# Revit family: v-180sz5(-n)_50Hz
name_source: partatom
category: 機械設備
units: mm (PartAtom-declared; Revit-internal decimal feet)

## family parameters
OmniClass タイトル = Centrifugal Fans
OmniClass 番号 = 23.75.35.17.27
パーツ タイプ = 標準
ロード時にボイドで切り取り = いいえ
丸型コネクタ寸法 = 直径を使用
作業面ベース = いいえ
共有 = いいえ
常に垂直 = はい
部屋計算ポイント = はい

## types (1)
- V-180SZU5-N
    Cover_Width = 132  [stored 0.433071 ft]
    D1 = 475  [stored 1.5584 ft]
    D2 = 120  [stored 0.393701 ft]
    Depth = 304  [stored 0.997375 ft]
    Duct_EA_Depth = 113  [stored 0.370735 ft]
    Duct_H = 116  [stored 0.380577 ft]
    Duct_RA_Depth1 = 198  [stored 0.649606 ft]
    Duct_RA_Depth2 = 322  [stored 1.05643 ft]
    Duct_RA_W1 = 113  [stored 0.370735 ft]
    EAサイズ_D = 98  [stored 0.321522 ft]
    Gril_D = 73  [stored 0.239501 ft]
    Gril_Depth = 146  [stored 0.479003 ft]
    Gril_W = 155  [stored 0.50853 ft]
    Gril_Width = 61  [stored 0.200131 ft]
    H1 = 12  [stored 0.0393701 ft]
    H2 = 198  [stored 0.649606 ft]
    Height = 211  [stored 0.692257 ft]
    IfcExportAs = IfcFanType
    IfcExportType = PROPELLORAXIAL
    MAX静圧 = 178.0 Pa
    MAX風量 = 225.0 m³/h
    MID静圧 = 0.0 Pa
    MID風量 = 0.0 m³/h
    MIN静圧 = 12.5 Pa
    MIN風量 = 60.0 m³/h
    OmniClassCode = 23-33 31 19 11 15
    Panel_W = 35  [stored 0.114829 ft]
    RAサイズ_D = 98  [stored 0.321522 ft]
    URL = https://www.mitsubishielectric.co.jp
    Uniclass2015Code = Pr_65_67_29_12
    Uniclass2015Title = Centrifugal fans
    Uniclass2015Version = Systems v1.9
    W1 = 475  [stored 1.5584 ft]
    W2 = 110  [stored 0.360892 ft]
    W3 = 152  [stored 0.498688 ft]
    Width = 304  [stored 0.997375 ft]
    カバーマテリアル = 合成樹脂(白)
    ダクト径 = 100 mm
    マテリアル = 合成樹脂(黒)
    モデル = V-180SZU5-N
    仕様書バージョン = Version1.0
    企業コード = 108420
    価格 = 109800 $
    分類コード = 50052503100050
    周波数 = 50 Hz
    極数 = 2
    法定耐用年数 = 15
    消費電力 = 48 W
    点検口 = はい
    相 = 1
    積算_科目 = 2 換気設備
    製品リリース年月 = 2022年6月1日
    製品出荷対象 = 国内
    製品質量 = 7.00 kg
    製造元 = 三菱電機株式会社
    設置方法 = 天埋
    説明 = エアフロー環気システム サニタリー換気ユニット 天井埋込形
    負荷分類 = 3_ファン類
    質量 = 8.40 kg
    運転質量 = 0.00 kg
    電動機出力 = 0 W
    電圧 = 100 V

note: [stored X ft] marks values corroborated as IEEE doubles in the binary element streams (Revit-internal decimal feet)
